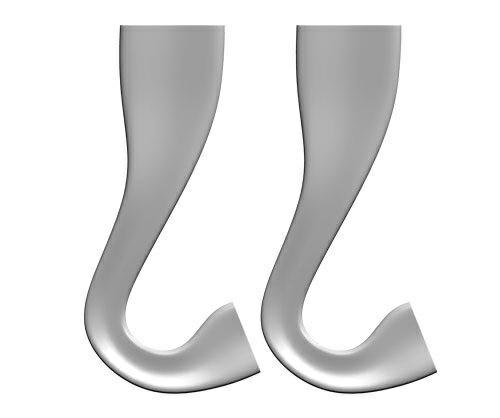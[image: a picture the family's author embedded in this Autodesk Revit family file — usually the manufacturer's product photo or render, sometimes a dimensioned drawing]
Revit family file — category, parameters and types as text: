
# Revit family: CITY ALPHABET letter „U”
name_source: partatom
category: Furniture
revit_build: Autodesk Revit 2018 (Build: 20190510_1515(x64)
units: mm (PartAtom-declared; Revit-internal decimal feet)

## family parameters
Cut with Voids When Loaded = No
Host = Face
OmniClass Number = 23.40.10.11.14
OmniClass Title = Exterior Seating
Room Calculation Point = No
Shared = No

## types (1)
- CITY ALPHABET letter „U”
    Default Elevation = 1219 mm
    Height = 420 mm  [stored 1.37795 ft]
    IfcExportAs = IfcFurnishingElement
    Length = 2250 mm
    Manufacturer = Astrini Design
    Material information = Colour choice from RAL colour standard. Customer may inquire about specific request regarding individual order.
    Model = CITY ALPHABET letter „U”
    Operating temperature = -40°C to 80°C, ( -40°F to 176°F )
    Type Comments = Bench
    Type Image = U.jpg
    URL = https://astrini-design.pl
    Weight (approximately) = 69.00 kg
    Weight - filled (approximately) = 169.00 kg
    Width = 2350 mm

note: [stored X ft] marks values corroborated as IEEE doubles in the binary element streams (Revit-internal decimal feet)
